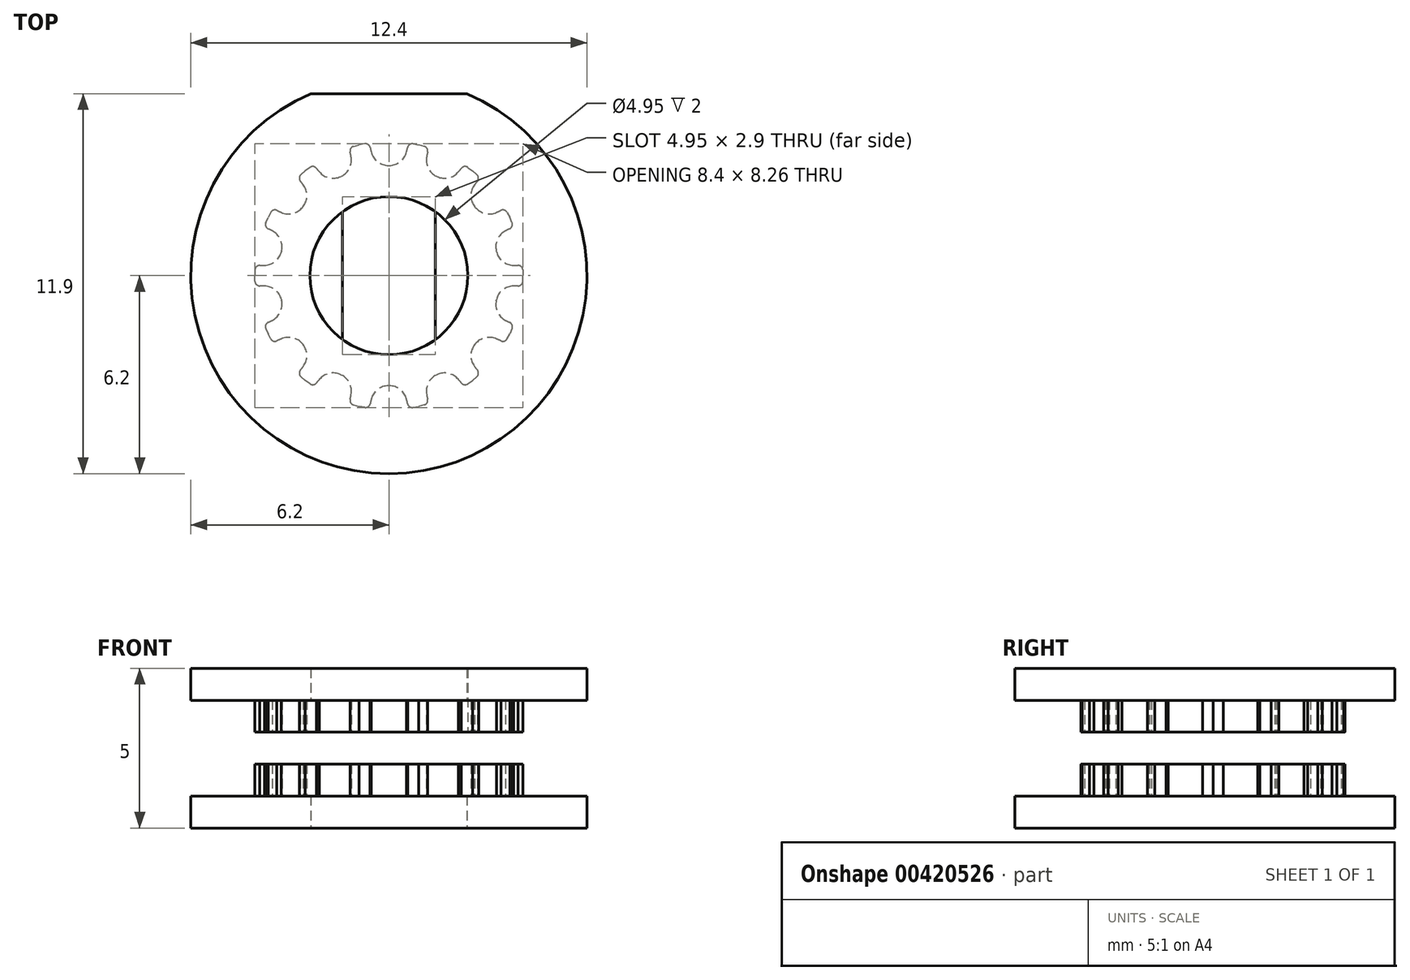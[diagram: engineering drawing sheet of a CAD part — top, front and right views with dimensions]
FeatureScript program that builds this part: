
annotation { "Feature Type Name" : "Feature", "Feature Type Description" : "" }
export const myFeature = defineFeature(function(context is Context, id is Id, definition is map)
    precondition{}
    {
        {
            assignVariable(context, id + "F0", {"name" : "teeth", "anyValue" : 14});
        }
        {
            var Q0;
            Q0=qCreatedBy(makeId("Top.planeOp"),FACE);
            var sketch = newSketch(context, id + "F1", { "sketchPlane" : qUnion([Q0])});
            skCircle(sketch, "E0", {"center": v(0, 0) * mm, "radius": 4.2 * mm, "construction": true});
            skLineSegment(sketch, "E1", {"start": v(0, 0) * mm, "end": v(0, 4.2) * mm, "construction": true});
            skLineSegment(sketch, "E2", {"start": v(0, 0) * mm, "end": v(0.93, 4.1) * mm, "construction": true});
            skArc(sketch, "E3", {"start": v(0.77, 3.36) * mm, "mid": v(0.39, 3.43) * mm, "end": v(0, 3.45) * mm, "construction": true});
            skArc(sketch, "E4", {"start": v(0.93, 4.1) * mm, "mid": v(0, 4.2) * mm, "end": v(-0.93, 4.1) * mm});
            skLineSegment(sketch, "E5", {"start": v(-0.93, 4.1) * mm, "end": v(-1.82, 8) * mm});
            skArc(sketch, "E6", {"start": v(1.82, 8) * mm, "mid": v(0, 8.2) * mm, "end": v(-1.82, 8) * mm});
            skLineSegment(sketch, "E7", {"start": v(1.82, 8) * mm, "end": v(0.93, 4.1) * mm});
            skLineSegment(sketch, "E8", {"start": v(0, 3.45) * mm, "end": v(0, 3.45) * mm});
            skLineSegment(sketch, "E9", {"start": v(0.55, 3.87) * mm, "end": v(0.59, 4.02) * mm, "construction": true});
            skLineSegment(sketch, "E10", {"start": v(0.76, 4.13) * mm, "end": v(0.93, 4.1) * mm});
            skPoint(sketch, "E11.visualSharp", {"position": v(0.62, 4.15) * mm});
            skArc(sketch, "E11.filletArc", {"start": v(0.76, 4.13) * mm, "mid": v(0.65, 4.1) * mm, "end": v(0.59, 4.02) * mm});
            skPoint(sketch, "E12.visualSharp", {"position": v(0.45, 3.45) * mm});
            skArc(sketch, "E12.filletArc", {"start": v(0, 3.45) * mm, "mid": v(0.35, 3.57) * mm, "end": v(0.55, 3.87) * mm});
            skArc(sketch, "E13.MirrorCS", {"start": v(0, 3.45) * mm, "mid": v(-0.35, 3.57) * mm, "end": v(-0.55, 3.87) * mm});
            skLineSegment(sketch, "E14.MirrorCS", {"start": v(-0.55, 3.87) * mm, "end": v(-0.59, 4.02) * mm, "construction": true});
            skArc(sketch, "E15.MirrorCS", {"start": v(-0.76, 4.13) * mm, "mid": v(-0.65, 4.1) * mm, "end": v(-0.59, 4.02) * mm});
            skLineSegment(sketch, "E16.MirrorCS", {"start": v(-0.76, 4.13) * mm, "end": v(-0.93, 4.1) * mm});
            skArc(sketch, "E17", {"start": v(0.55, 3.87) * mm, "mid": v(0.57, 3.94) * mm, "end": v(0.59, 4.02) * mm});
            skArc(sketch, "E18.MirrorCS", {"start": v(-0.55, 3.87) * mm, "mid": v(-0.57, 3.94) * mm, "end": v(-0.59, 4.02) * mm});
            skSolve(sketch);
        }
        {
            var Q0;
            Q0=qCreatedBy(makeId("Top.planeOp"),FACE);
            var sketch = newSketch(context, id + "F2", { "sketchPlane" : qUnion([Q0])});
            skCircle(sketch, "E19", {"center": v(0, 0) * mm, "radius": 6.2 * mm});
            skCircle(sketch, "E20", {"center": v(0, 0) * mm, "radius": 2.48 * mm});
            skLineSegment(sketch, "E21", {"start": v(-1.45, 2) * mm, "end": v(-1.45, -2) * mm});
            skLineSegment(sketch, "E22", {"start": v(1.45, 2) * mm, "end": v(1.45, -2) * mm});
            skCircle(sketch, "E23", {"center": v(-4.47, 0) * mm, "radius": 0.5 * mm, "construction": true});
            skCircle(sketch, "E24", {"center": v(4.47, 0) * mm, "radius": 0.5 * mm, "construction": true});
            skLineSegment(sketch, "E25", {"start": v(-4.47, 0) * mm, "end": v(4.47, 0) * mm, "construction": true});
            skLineSegment(sketch, "E26", {"start": v(-2.44, 5.7) * mm, "end": v(2.44, 5.7) * mm});
            skSolve(sketch);
        }
        {
            var Q0;
            Q0=makeQuery(id+"F2.imprint","IMPRINT",FACE,{"disambiguationData":[TD([[makeQuery(id+"F2.imprint","IMPRINT",EDGE,{"derivedFrom":sQuery(id+"F2.wireOp",EDGE,"E23")}),-1.0]])]});
            var Q1;
            {var subQ7=sQuery(id+"F2.wireOp",EDGE,"E26");Q1=makeQuery(id+"F2.imprint","IMPRINT",FACE,{"disambiguationData":[TD([[makeQuery(id+"F2.imprint","IMPRINT",EDGE,{"derivedFrom":subQ7}),-1.0]])]});}
            extrude(context, id + "F3", {"entities" : qUnion([Q0, Q1]), "depth" : 2.5 * mm, "offsetDistance" : 25 * mm});
        }
        {
            var Q0;
            {var subQ7=sQuery(id+"F2.wireOp",EDGE,"E26");Q0=makeQuery(id+"F2.imprint","IMPRINT",FACE,{"disambiguationData":[TD([[makeQuery(id+"F2.imprint","IMPRINT",EDGE,{"derivedFrom":subQ7}),-1.0]])]});}
            var Q1;
            {var subQ0=sQuery(id+"F2.wireOp",EDGE,"E21");Q1=makeQuery(id+"F2.imprint","IMPRINT",FACE,{"disambiguationData":[TD([[makeQuery(id+"F2.imprint","IMPRINT",EDGE,{"derivedFrom":subQ0}),-1.0]])]});}
            var Q2;
            {var subQ0=sQuery(id+"F2.wireOp",EDGE,"E22");Q2=makeQuery(id+"F2.imprint","IMPRINT",FACE,{"disambiguationData":[TD([[makeQuery(id+"F2.imprint","IMPRINT",EDGE,{"derivedFrom":subQ0}),1.0]])]});}
            extrude(context, id + "F4", {"entities" : qUnion([Q0, Q1, Q2]), "operationType" : NewBodyOperationType.ADD, "oppositeDirection" : true, "depth" : 2.5 * mm, "offsetDistance" : 25 * mm});
        }
        {
            var Q0;
            Q0=qSketchRegion(id+"F1",true);
            extrude(context, id + "F5", {"entities" : qUnion([Q0]), "endBound" : BoundingType.SYMMETRIC, "depth" : 3 * mm, "offsetDistance" : 25 * mm});
        }
        {
            var Q0;
            Q0=makeQuery(id+"F5.opExtrude","SWEPT_BODY",BODY,{"disambiguationData":[OSD([sQuery(id+"F1.wireOp",EDGE,"a4fd81c2-d7e9-4ebd-908a-522a74531fd4"),sQuery(id+"F1.wireOp",EDGE,"bb5d716b-bc2b-4b1a-a15f-9d956a1bf7b70.MirrorCS"),sQuery(id+"F1.wireOp",EDGE,"E4")])]});
            var Q1;
            Q1=makeQuery(id+"F5.opExtrude","SWEPT_BODY",BODY,{"disambiguationData":[OSD([sQuery(id+"F1.wireOp",EDGE,"E5"),sQuery(id+"F1.wireOp",EDGE,"E6"),sQuery(id+"F1.wireOp",EDGE,"E7"),sQuery(id+"F1.wireOp",EDGE,"E8"),sQuery(id+"F1.wireOp",EDGE,"E9"),sQuery(id+"F1.wireOp",EDGE,"E10"),sQuery(id+"F1.wireOp",EDGE,"E11.filletArc"),sQuery(id+"F1.wireOp",EDGE,"E12.filletArc"),sQuery(id+"F1.wireOp",EDGE,"E13.MirrorCS"),sQuery(id+"F1.wireOp",EDGE,"E14.MirrorCS"),sQuery(id+"F1.wireOp",EDGE,"E15.MirrorCS"),sQuery(id+"F1.wireOp",EDGE,"E16.MirrorCS"),sQuery(id+"F1.wireOp",EDGE,"E8")])]});
            var Q2;
            Q2=sQuery(id+"F1.wireOp",EDGE,"E0");
            circularPattern(context, id + "F6", {"operationType" : NewBodyOperationType.REMOVE, "entities" : qUnion([Q0, Q1]), "axis" : qUnion([Q2]), "angle" : 360 * degree, "instanceCount" : getVariable(context, 'teeth'), "equalSpace" : true});
        }
        {
            var Q0;
            Q0=qSketchRegion(id+"F2",true);
            var Q1;
            {var subQ0=sQuery(id+"F2.wireOp",EDGE,"E22");Q1=makeQuery(id+"F2.imprint","IMPRINT",FACE,{"disambiguationData":[TD([[makeQuery(id+"F2.imprint","IMPRINT",EDGE,{"derivedFrom":subQ0}),1.0]])]});}
            var Q2;
            {var subQ0=sQuery(id+"F2.wireOp",EDGE,"E21");Q2=makeQuery(id+"F2.imprint","IMPRINT",FACE,{"disambiguationData":[TD([[makeQuery(id+"F2.imprint","IMPRINT",EDGE,{"derivedFrom":subQ0}),1.0]])]});}
            var Q3;
            {var subQ0=sQuery(id+"F2.wireOp",EDGE,"E21");Q3=makeQuery(id+"F2.imprint","IMPRINT",FACE,{"disambiguationData":[TD([[makeQuery(id+"F2.imprint","IMPRINT",EDGE,{"derivedFrom":subQ0}),-1.0]])]});}
            extrude(context, id + "F7", {"entities" : qUnion([Q0, Q1, Q2, Q3]), "operationType" : NewBodyOperationType.REMOVE, "endBound" : BoundingType.SYMMETRIC, "oppositeDirection" : true, "depth" : 1 * mm, "offsetDistance" : 25 * mm});
        }
        {
            var Q0;
            Q0=makeQuery(id+"F7.boolean.opBoolean","SPLIT",BODY,{"disambiguationData":[OD(0.0)],"derivedFrom":makeQuery(id+"F3.opExtrude","SWEPT_BODY",BODY,{"disambiguationData":[OSD([sQuery(id+"F2.wireOp",EDGE,"E19"),sQuery(id+"F2.wireOp",EDGE,"E20"),sQuery(id+"F2.wireOp",EDGE,"E21"),sQuery(id+"F2.wireOp",EDGE,"E22")])]})});
            transform(context, id + "F8", {"entities" : qUnion([Q0]), "transformType" : TransformType.TRANSLATION_3D, "dx" : 0 * mm, "dy" : 0 * mm, "dz" : -10 * mm, "makeCopy" : false});
        }
    });
